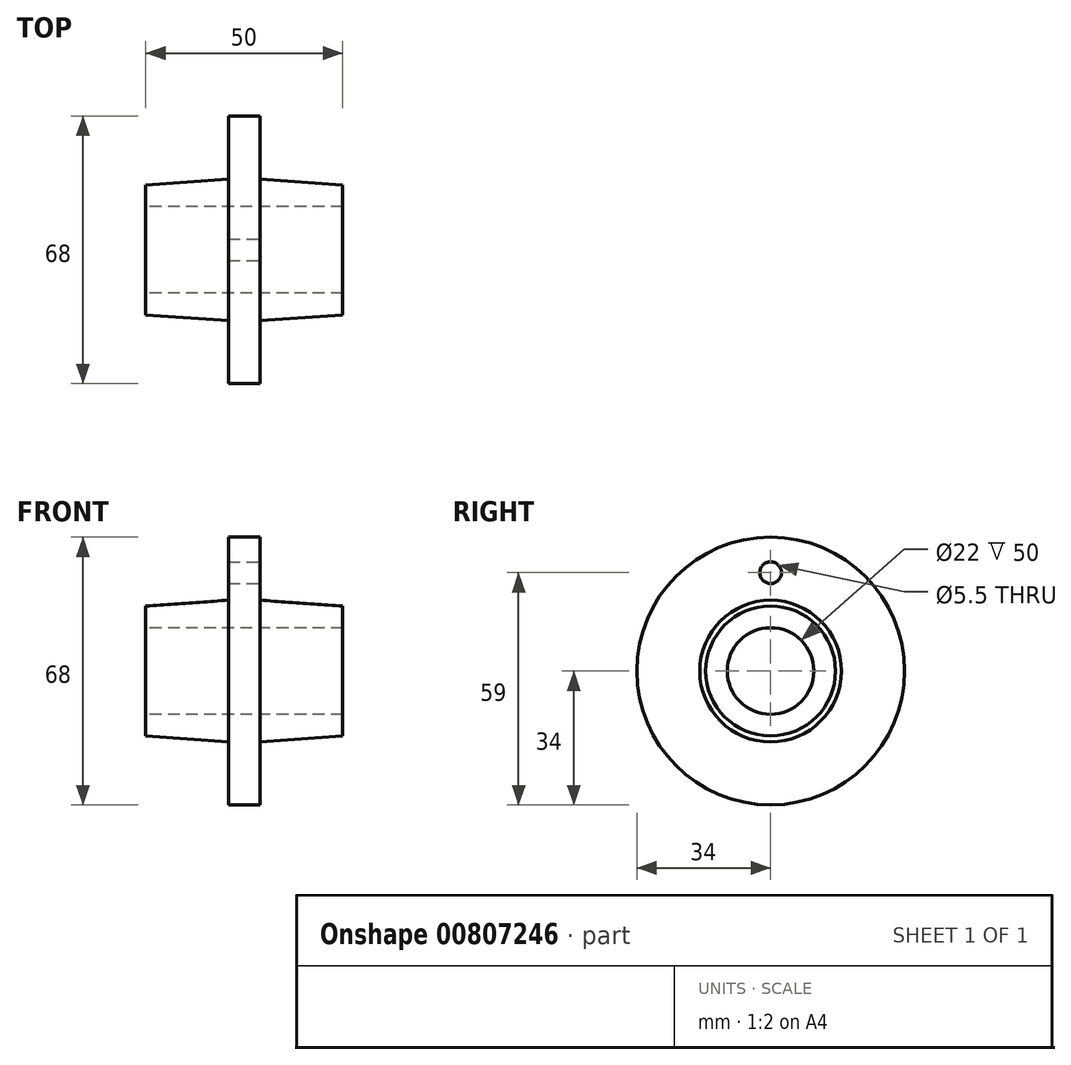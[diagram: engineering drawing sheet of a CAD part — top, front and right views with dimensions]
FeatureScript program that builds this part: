
annotation { "Feature Type Name" : "Feature", "Feature Type Description" : "" }
export const myFeature = defineFeature(function(context is Context, id is Id, definition is map)
    precondition{}
    {
        {
            var Q0;
            Q0=qCreatedBy(makeId("Front.planeOp"),FACE);
            var sketch = newSketch(context, id + "F0", { "sketchPlane" : qUnion([Q0])});
            skLineSegment(sketch, "E0", {"start": v(-41.68, 0) * mm, "end": v(35.9, 0) * mm, "construction": true});
            skLineSegment(sketch, "E1", {"start": v(0, -9.87) * mm, "end": v(0, 0) * mm, "construction": true});
            skLineSegment(sketch, "E2", {"start": v(-25, 11) * mm, "end": v(25, 11) * mm});
            skLineSegment(sketch, "E3", {"start": v(25, 11) * mm, "end": v(25, 16.5) * mm});
            skLineSegment(sketch, "E4", {"start": v(25, 16.5) * mm, "end": v(4, 18) * mm});
            skLineSegment(sketch, "E5", {"start": v(4, 18) * mm, "end": v(4, 34) * mm});
            skLineSegment(sketch, "E6", {"start": v(4, 34) * mm, "end": v(-4, 34) * mm});
            skLineSegment(sketch, "E7", {"start": v(-4, 34) * mm, "end": v(-4, 18) * mm});
            skLineSegment(sketch, "E8", {"start": v(-4, 18) * mm, "end": v(-25, 16.5) * mm});
            skLineSegment(sketch, "E9", {"start": v(-25, 16.5) * mm, "end": v(-25, 11) * mm});
            skSolve(sketch);
        }
        {
            var Q0;
            Q0 = qSketchRegion(id + "F0", true);
            var Q1;
            Q1=sQuery(id+"F0.wireOp",EDGE,"E0");
            revolve(context, id + "F1", {"surfaceOperationType" : NewSurfaceOperationType.NEW, "entities" : qUnion([Q0]), "axis" : qUnion([Q1]), "revolveType" : RevolveType.FULL});
        }
        {
            var Q0;
            Q0=makeQuery(id+"F1.opRevolve","SWEPT_FACE",FACE,{"disambiguationData":[OSD([sQuery(id+"F0.wireOp",EDGE,"E5")])]});
            var sketch = newSketch(context, id + "F2", { "sketchPlane" : qUnion([Q0])});
            skCircle(sketch, "E10", {"center": v(0, 0) * mm, "radius": 25 * mm, "construction": true});
            skPoint(sketch, "E11", {"position": v(0, 25) * mm});
            skSolve(sketch);
        }
        {
            var Q0;
            Q0=sQuery(id+"F2.wireOp",VERTEX,"E11");
            var Q1;
            Q1=makeQuery(id+"F1.opRevolve","SWEPT_BODY",BODY,{"disambiguationData":[OSD([sQuery(id+"F0.wireOp",EDGE,"E2"),sQuery(id+"F0.wireOp",EDGE,"E3"),sQuery(id+"F0.wireOp",EDGE,"E4"),sQuery(id+"F0.wireOp",EDGE,"E5"),sQuery(id+"F0.wireOp",EDGE,"E6"),sQuery(id+"F0.wireOp",EDGE,"E7"),sQuery(id+"F0.wireOp",EDGE,"E8"),sQuery(id+"F0.wireOp",EDGE,"E9")])]});
            hole(context, id + "F3", {"style" : HoleStyle.SIMPLE, "endStyle" : HoleEndStyle.THROUGH, "holeDiameter" : 5.5 * mm, "majorDiameter" : 5 * mm, "tappedDepth" : 12 * mm, "tapClearance" : 3, "startFromSketch" : true, "locations" : qUnion([Q0]), "scope" : qUnion([Q1])});
        }
    });
